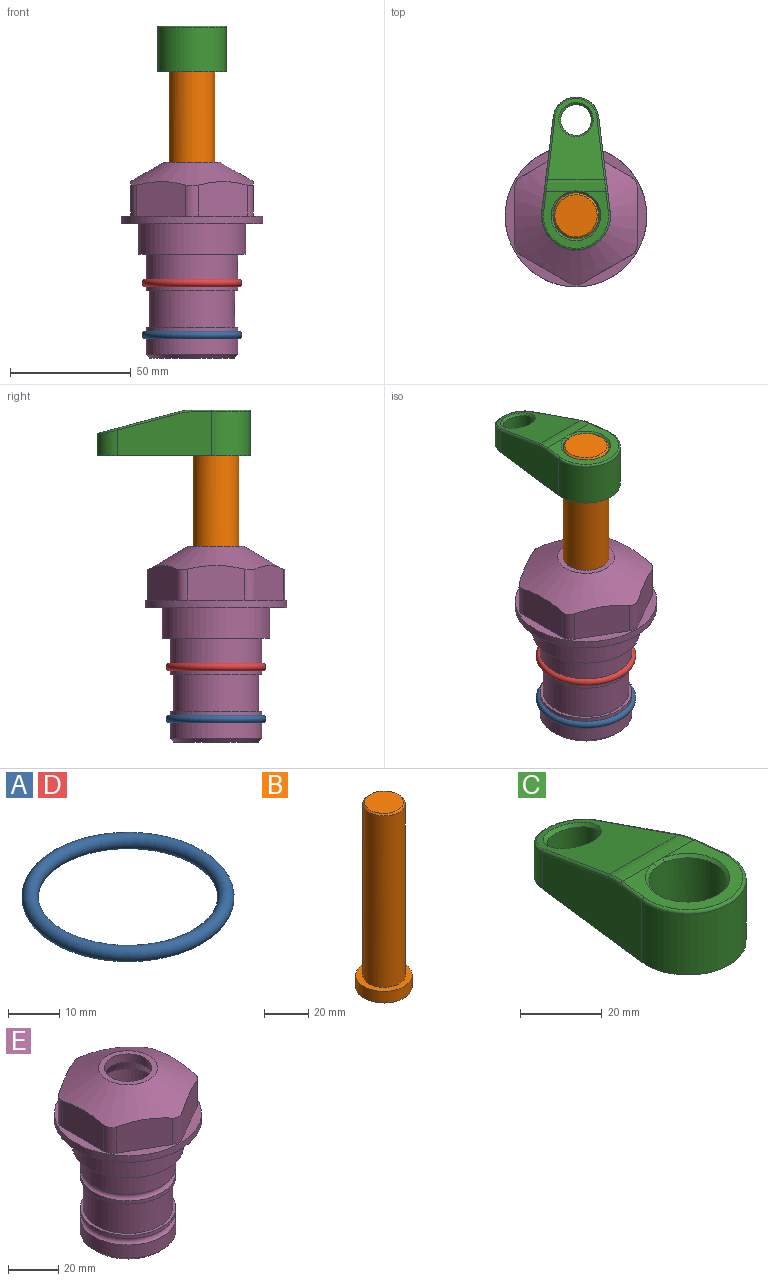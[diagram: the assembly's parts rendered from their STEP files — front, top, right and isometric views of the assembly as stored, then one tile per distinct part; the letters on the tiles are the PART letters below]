
ASSEMBLY  parts=5 mates=4
PART A: 1 faces, bbox 44.7x44.7x3.2 mm
  f0: torus R=19.05mm, axis (0,0,1), area 1193.9mm2
PART B: 6 faces, bbox 25.4x25.4x101.6 mm
  f0: plane 17.46x17.46mm, normal (0,0,1), area 239.5mm2, adj f5
  f1: plane 25.4x25.4mm, normal (0,0,-1), area 506.7mm2, adj f2
  f2: cylinder r=12.7mm len=25.4mm, axis (0,0,1), area 506.7mm2, adj f1,f3
  f3: plane 25.4x25.4mm, normal (0,0,1), area 221.7mm2, adj f2,f4
  f4: cylinder r=9.53mm len=94.46mm, axis (0,0,1), area 5653mm2, adj f3,f5
  f5: cone r=8.73mm half-angle=45deg, axis (0,0,-1), area 64.4mm2, adj f0,f4
PART C: 31 faces, bbox 31.7x65.5x19.8 mm
  f0: plane 39.12x18.26mm, normal (0.99,0.12,0), area 612.2mm2, adj f1,f4,f7,f11,f13,f15
  f1: cylinder r=9.53mm len=18.91mm, axis (0,0,-1), area 296.1mm2, adj f0,f2,f7,f17
  f2: plane 39.12x18.26mm, normal (-0.99,0.12,0), area 612.2mm2, adj f1,f4,f7,f12,f14,f16
  f3: cylinder r=6.35mm len=12.7mm, axis (0,0,-1), area 362.4mm2, adj f7,f18
  f4: cylinder r=14.29mm len=28.58mm, axis (0,0,-1), area 882.2mm2, adj f0,f2,f7,f10
  f5: cylinder r=9.53mm len=19.05mm, axis (0,0,-1), area 1092.6mm2, adj f7,f19,f20
  f6: plane 26.99x23.69mm, normal (0,0,1), area 216.2mm2, adj f9,f10,f11,f12,f19
  f7: plane 63.5x28.58mm, normal (0,0,-1), area 661.8mm2, adj f0,f1,f2,f3,f4,f5,f22,f23
  f8: plane 33.52x23.6mm, normal (0,0.26,0.97), area 486mm2, adj f9,f15,f16,f17,f18
  f9: cylinder r=19.05mm len=24.72mm, axis (1,0,0), area 120.4mm2, adj f6,f8,f13,f14,f20
  f10: torus R=13.49mm, axis (0,0,1), area 59mm2, adj f4,f6,f11,f12
  f11: cylinder r=0.79mm len=8.67mm, axis (0.12,-0.99,0), area 10.8mm2, adj f0,f6,f10,f13
  f12: cylinder r=0.79mm len=8.67mm, axis (0.12,0.99,0), area 10.8mm2, adj f2,f6,f10,f14
  f13: bspline ~4.95x1.42mm, area 6.1mm2, adj f0,f9,f11,f15
  f14: bspline ~4.95x1.42mm, area 6.1mm2, adj f2,f9,f12,f16
  f15: cylinder r=0.79mm len=25.95mm, axis (0.12,-0.96,0.26), area 32.9mm2, adj f0,f8,f13,f17
  f16: cylinder r=0.79mm len=25.95mm, axis (0.12,0.96,-0.26), area 32.9mm2, adj f2,f8,f14,f17
  f17: bspline ~18.91x8.38mm, area 30mm2, adj f1,f8,f15,f16
  f18: bspline ~14.29x14.29mm, area 48.3mm2, adj f3,f8
  f19: cone r=9.53mm half-angle=45deg, axis (0,0,1), area 66.5mm2, adj f5,f6,f20
  f20: bspline ~3.22x0.96mm, area 3.5mm2, adj f5,f9,f19
  f21: plane 2.75x2.72mm, normal (0,0,-1), area 2.9mm2, adj f23,f25,f28
  f22: plane 23.05x15.88mm, normal (-0.99,-0.12,0), area 323.6mm2, adj f7,f25,f26,f27,f28,f29
  f23: plane 23.05x15.88mm, normal (0.99,-0.12,0), area 323.6mm2, adj f7,f21,f25,f27,f28,f30
  f24: cylinder r=9.53mm len=10.69mm, axis (0,0,-1), area 114.7mm2, adj f7,f27,f29,f30
  f25: cylinder r=12.7mm len=20.59mm, axis (0,0,-1), area 381.1mm2, adj f7,f21,f22,f23,f26,f28
  f26: plane 2.75x2.72mm, normal (0,0,-1), area 2.9mm2, adj f22,f25,f28
  f27: plane 19.72x18.37mm, normal (0,-0.26,-0.97), area 291.8mm2, adj f22,f23,f24,f28,f29,f30
  f28: cylinder r=15.88mm len=19.92mm, axis (1,0,0), area 54.8mm2, adj f21,f22,f23,f25,f26,f27
  f29: cylinder r=1.59mm len=11mm, axis (0,0,-1), area 34.7mm2, adj f7,f22,f24,f27
  f30: cylinder r=1.59mm len=11mm, axis (0,0,-1), area 34.7mm2, adj f7,f23,f24,f27
PART D: same geometry as A
PART E: 36 faces, bbox 58.7x58.7x81 mm
  f0: cylinder r=17.78mm len=35.56mm, axis (0,0,1), area 1670.8mm2, adj f23,f24,f31
  f1: cylinder r=19.05mm len=38.1mm, axis (0,0,1), area 1191.9mm2, adj f26,f27,f30
  f2: plane 58.66x58.66mm, normal (0,0,-1), area 1150.6mm2, adj f3,f28
  f3: cylinder r=29.33mm len=58.66mm, axis (0,0,-1), area 585.1mm2, adj f2,f4
  f4: plane 58.66x58.66mm, normal (0,0,1), area 475.9mm2, adj f3,f5,f6,f7,f8,f9,f10,f11
  f5: plane 20.32x14.34mm, normal (-0.5,0.87,0), area 324.4mm2, adj f4,f15,f16,f17
  f6: plane 20.32x14.34mm, normal (0.5,0.87,0), area 324.4mm2, adj f4,f14,f15,f17
  f7: plane 23.48x14.34mm, normal (1,0,0), area 324.4mm2, adj f4,f13,f14,f17
  f8: plane 20.32x14.34mm, normal (0.5,-0.87,0), area 324.4mm2, adj f4,f12,f13,f17
  f9: plane 20.32x14.34mm, normal (-0.5,-0.87,0), area 324.4mm2, adj f4,f11,f12,f17
  f10: plane 23.48x14.34mm, normal (-1,0,0), area 324.4mm2, adj f4,f11,f16,f17
  f11: cylinder r=5.08mm len=12.85mm, axis (0,0,-1), area 67.2mm2, adj f4,f9,f10,f17
  f12: cylinder r=5.08mm len=12.85mm, axis (0,0,-1), area 67.2mm2, adj f4,f8,f9,f17
  f13: cylinder r=5.08mm len=12.85mm, axis (0,0,-1), area 67.2mm2, adj f4,f7,f8,f17
  f14: cylinder r=5.08mm len=12.85mm, axis (0,0,-1), area 67.2mm2, adj f4,f6,f7,f17
  f15: cylinder r=5.08mm len=12.85mm, axis (0,0,-1), area 67.2mm2, adj f4,f5,f6,f17
  f16: cylinder r=5.08mm len=12.85mm, axis (0,0,-1), area 67.2mm2, adj f4,f5,f10,f17
  f17: cone r=11.73mm half-angle=60deg, axis (0,0,-1), area 2071.8mm2, adj f5,f6,f7,f8,f9,f10,f11,f12
  f18: plane 23.46x23.46mm, normal (0,0,1), area 147.4mm2, adj f17,f35
  f19: plane 34.93x34.93mm, normal (0,0,-1), area 958mm2, adj f29
  f20: cylinder r=19.05mm len=38.1mm, axis (0,0,1), area 760.1mm2, adj f21,f29
  f21: torus R=19.05mm, axis (0,0,1), area 565.3mm2, adj f20,f22
  f22: cylinder r=19.05mm len=38.1mm, axis (0,0,1), area 190mm2, adj f21,f23
  f23: plane 38.1x38.1mm, normal (0,0,1), area 146.9mm2, adj f0,f22
  f24: plane 38.1x38.1mm, normal (0,0,-1), area 146.9mm2, adj f0,f25
  f25: cylinder r=19.05mm len=38.1mm, axis (0,0,1), area 190mm2, adj f24,f26
  f26: torus R=19.05mm, axis (0,0,1), area 565.3mm2, adj f1,f25
  f27: plane 44.45x44.45mm, normal (0,0,-1), area 411.7mm2, adj f1,f28
  f28: cylinder r=22.23mm len=44.45mm, axis (0,0,1), area 1773.5mm2, adj f2,f27
  f29: cone r=19.05mm half-angle=45deg, axis (0,0,1), area 257.5mm2, adj f19,f20
  f30: cylinder r=3.17mm len=6.75mm, axis (-1,0,0), area 128mm2, adj f1,f33
  f31: cylinder r=3.17mm len=6.35mm, axis (-1,0,0), area 102.5mm2, adj f0,f33
  f32: plane 25.4x25.4mm, normal (0,0,1), area 506.7mm2, adj f33
  f33: cylinder r=12.7mm len=66.42mm, axis (0,0,-1), area 5236.2mm2, adj f30,f31,f32,f34
  f34: cone r=9.53mm half-angle=30deg, axis (0,0,-1), area 443.4mm2, adj f33,f35
  f35: cylinder r=9.53mm len=19.05mm, axis (0,0,-1), area 240.9mm2, adj f18,f34
PLACE A t=(0,0,-21.59)mm
PLACE B t=(0,0,18.45)mm
PLACE C t=(0,0,18.45)mm
PLACE D at identity
PLACE E at identity fixed
MATE fastened D.f0 <-> E.f0  axis (0,0,1) through (0,0,-24.51)mm
MATE fastened A.f0 <-> E.f0  axis (0,0,1) through (0,0,-46.1)mm
MATE fastened C.f4 <-> B.f2  axis (0,0,1) through (0,0,81.95)mm
MATE cylindrical B.f2 <-> E.f0  axis (0,0,-1) through (0,0,-19.65)mm
